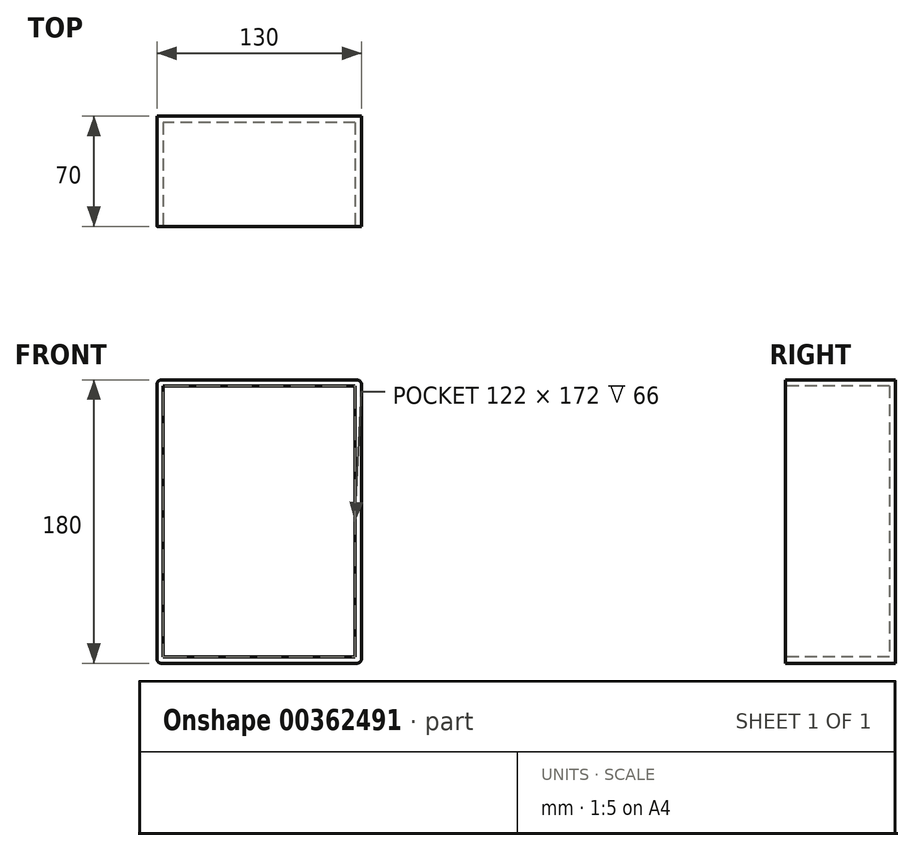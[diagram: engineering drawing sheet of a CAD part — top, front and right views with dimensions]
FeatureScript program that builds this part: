
annotation { "Feature Type Name" : "Feature", "Feature Type Description" : "" }
export const myFeature = defineFeature(function(context is Context, id is Id, definition is map)
    precondition{}
    {
        {
            var Q0;
            Q0=qCreatedBy(makeId("Front.planeOp"),FACE);
            var sketch = newSketch(context, id + "F0", { "sketchPlane" : qUnion([Q0])});
            skLineSegment(sketch, "E0.bottom", {"start": v(18.12, 100.72) * mm, "end": v(148.12, 100.72) * mm});
            skLineSegment(sketch, "E0.top", {"start": v(18.12, -79.28) * mm, "end": v(148.12, -79.28) * mm});
            skLineSegment(sketch, "E0.left", {"start": v(18.12, 100.72) * mm, "end": v(18.12, -79.28) * mm});
            skLineSegment(sketch, "E0.right", {"start": v(148.12, 100.72) * mm, "end": v(148.12, -79.28) * mm});
            skSolve(sketch);
        }
        {
            var Q0;
            Q0=makeQuery(id+"F0.imprint","IMPRINT",FACE,{"disambiguationData":[TD([[makeQuery(id+"F0.imprint","IMPRINT",EDGE,{"derivedFrom":sQuery(id+"F0.wireOp",EDGE,"E0.bottom")}),-1.0]])]});
            extrude(context, id + "F1", {"entities" : qUnion([Q0]), "depth" : 70 * mm});
        }
        {
            var Q0;
            Q0=makeQuery(id+"F1.opExtrude","CAP_FACE",FACE,{"disambiguationData":[OSD([sQuery(id+"F0.wireOp",EDGE,"E0.bottom"),sQuery(id+"F0.wireOp",EDGE,"E0.top"),sQuery(id+"F0.wireOp",EDGE,"E0.left"),sQuery(id+"F0.wireOp",EDGE,"E0.right")])],"isStart":false});
            var sketch = newSketch(context, id + "F2", { "sketchPlane" : qUnion([Q0])});
            skLineSegment(sketch, "E1.0", {"start": v(22.12, 96.72) * mm, "end": v(22.12, -75.28) * mm});
            skLineSegment(sketch, "E1.1", {"start": v(144.12, 96.72) * mm, "end": v(22.12, 96.72) * mm});
            skLineSegment(sketch, "E1.2", {"start": v(144.12, -75.28) * mm, "end": v(144.12, 96.72) * mm});
            skLineSegment(sketch, "E1.3", {"start": v(22.12, -75.28) * mm, "end": v(144.12, -75.28) * mm});
            skSolve(sketch);
        }
        {
            var Q0;
            Q0=makeQuery(id+"F2.imprint","IMPRINT",FACE,{"disambiguationData":[TD([[makeQuery(id+"F2.imprint","IMPRINT",EDGE,{"derivedFrom":sQuery(id+"F2.wireOp",EDGE,"E1.0")}),1.0]])]});
            extrude(context, id + "F3", {"entities" : qUnion([Q0]), "operationType" : NewBodyOperationType.REMOVE, "oppositeDirection" : true, "depth" : 66 * mm});
        }
        {
            var Q0;
            Q0=makeQuery(id+"F1.opExtrude","SWEPT_EDGE",EDGE,{"disambiguationData":[OSD([sQuery(id+"F0.wireOp",EDGE,"E0.bottom"),sQuery(id+"F0.wireOp",EDGE,"E0.left")])]});
            var Q1;
            Q1=makeQuery(id+"F1.opExtrude","SWEPT_EDGE",EDGE,{"disambiguationData":[OSD([sQuery(id+"F0.wireOp",EDGE,"E0.bottom"),sQuery(id+"F0.wireOp",EDGE,"E0.right")])]});
            var Q2;
            Q2=makeQuery(id+"F1.opExtrude","SWEPT_EDGE",EDGE,{"disambiguationData":[OSD([sQuery(id+"F0.wireOp",EDGE,"E0.top"),sQuery(id+"F0.wireOp",EDGE,"E0.left")])]});
            var Q3;
            Q3=makeQuery(id+"F1.opExtrude","SWEPT_EDGE",EDGE,{"disambiguationData":[OSD([sQuery(id+"F0.wireOp",EDGE,"E0.top"),sQuery(id+"F0.wireOp",EDGE,"E0.right")])]});
            fillet(context, id + "F4", {"entities" : qUnion([Q0, Q1, Q2, Q3]), "radius" : 3 * mm, "tangentPropagation" : true, "allowEdgeOverflow" : false});
        }
    });
